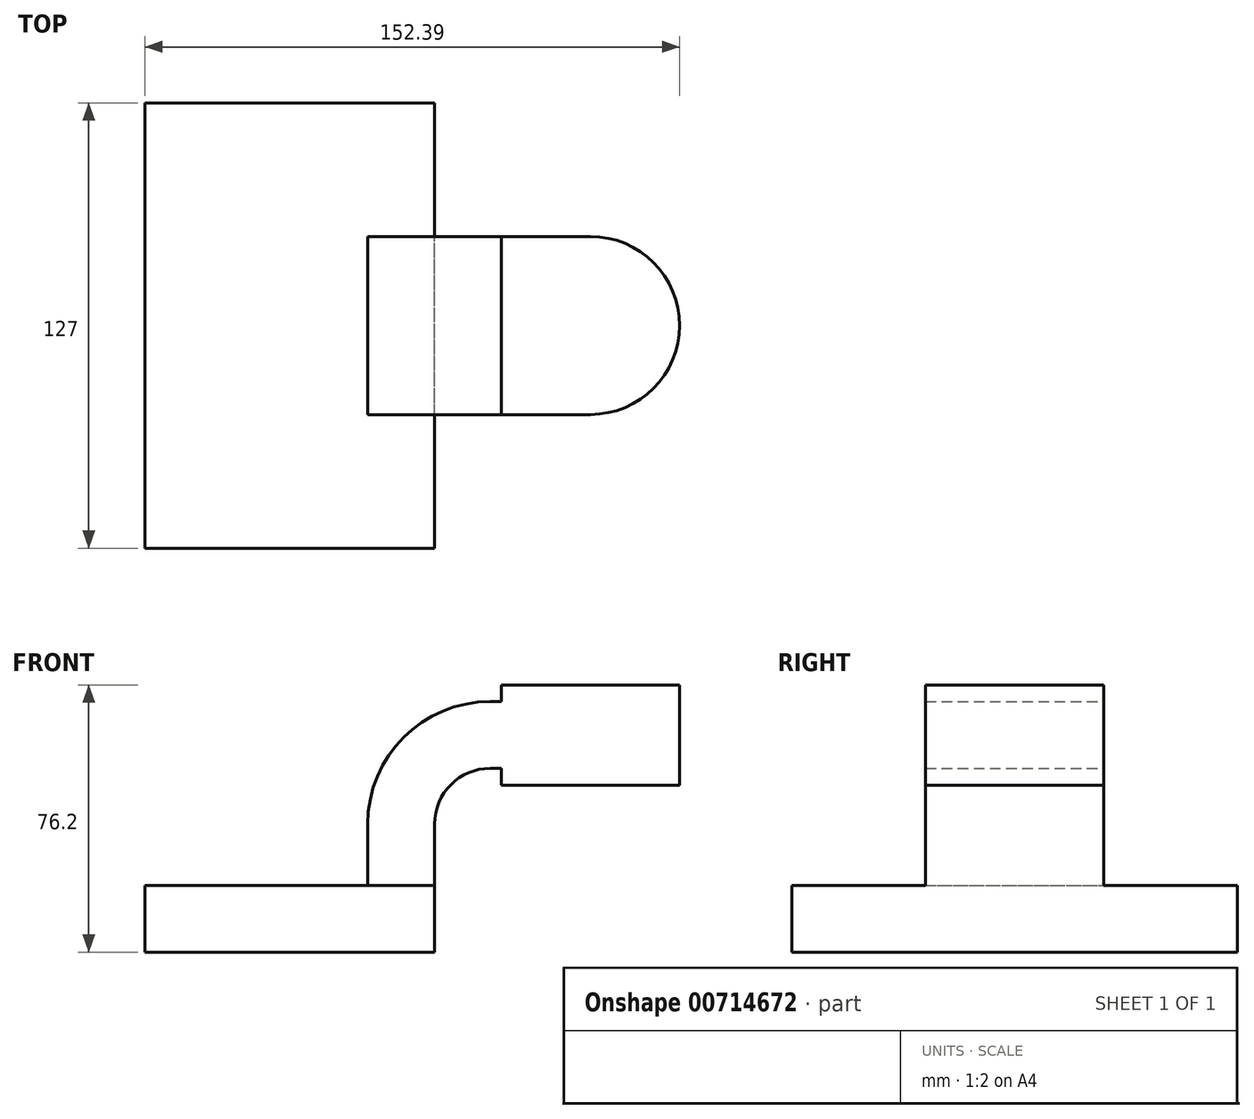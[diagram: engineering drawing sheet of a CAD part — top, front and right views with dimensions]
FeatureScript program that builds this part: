
annotation { "Feature Type Name" : "Feature", "Feature Type Description" : "" }
export const myFeature = defineFeature(function(context is Context, id is Id, definition is map)
    precondition{}
    {
        {
            var Q0;
            Q0=qCreatedBy(makeId("Front.planeOp"),FACE);
            var sketch = newSketch(context, id + "F0", { "sketchPlane" : qUnion([Q0])});
            skLineSegment(sketch, "E0.bottom", {"start": v(-41.28, -9.53) * mm, "end": v(41.28, -9.53) * mm});
            skLineSegment(sketch, "E0.top", {"start": v(-41.28, 9.53) * mm, "end": v(41.28, 9.53) * mm});
            skLineSegment(sketch, "E0.left", {"start": v(-41.28, -9.53) * mm, "end": v(-41.28, 9.53) * mm});
            skLineSegment(sketch, "E0.right", {"start": v(41.28, -9.53) * mm, "end": v(41.28, 9.53) * mm});
            skPoint(sketch, "E0.middle", {"position": v(0, 0) * mm});
            skLineSegment(sketch, "E1.bottom", {"start": v(60.32, 38.1) * mm, "end": v(111.12, 38.1) * mm});
            skLineSegment(sketch, "E1.top", {"start": v(60.32, 66.68) * mm, "end": v(111.12, 66.68) * mm});
            skLineSegment(sketch, "E1.left", {"start": v(60.32, 38.1) * mm, "end": v(60.32, 66.67) * mm});
            skLineSegment(sketch, "E1.right", {"start": v(111.12, 38.1) * mm, "end": v(111.12, 66.67) * mm});
            skPoint(sketch, "E1.middle", {"position": v(85.72, 52.39) * mm});
            skLineSegment(sketch, "E2", {"start": v(41.28, 9.53) * mm, "end": v(41.28, 27) * mm});
            skArc(sketch, "E3", {"start": v(41.27, 27) * mm, "mid": v(45.92, 38.23) * mm, "end": v(57.15, 42.88) * mm});
            skLineSegment(sketch, "E4", {"start": v(57.15, 42.88) * mm, "end": v(85.25, 42.88) * mm});
            skLineSegment(sketch, "E5.0", {"start": v(57.15, 61.93) * mm, "end": v(85.25, 61.93) * mm});
            skArc(sketch, "E5.1", {"start": v(22.22, 27) * mm, "mid": v(32.45, 51.7) * mm, "end": v(57.15, 61.93) * mm});
            skLineSegment(sketch, "E5.2", {"start": v(22.23, 9.53) * mm, "end": v(22.23, 27) * mm});
            skLineSegment(sketch, "E6", {"start": v(85.72, 66.68) * mm, "end": v(85.72, 38.1) * mm});
            skFitSpline(sketch, "E7", {"points": [v(-41.28, 9.53) * mm, v(60.32, 66.67) * mm], "startDerivative": vector(64.63, 87.24) * mm, "endDerivative": vector(129.97, 21.04) * mm});
            skSolve(sketch);
        }
        {
            var Q0;
            Q0=makeQuery(id+"F0.imprint","IMPRINT",FACE,{"disambiguationData":[TD([[makeQuery(id+"F0.imprint","IMPRINT",EDGE,{"derivedFrom":sQuery(id+"F0.wireOp",EDGE,"E0.bottom")}),1.0]])]});
            extrude(context, id + "F1", {"entities" : qUnion([Q0]), "endBound" : BoundingType.SYMMETRIC, "depth" : 127 * mm, "offsetDistance" : 25.4 * mm});
        }
        {
            var Q0;
            {var subQ1=sQuery(id+"F0.wireOp",EDGE,"E2");Q0=makeQuery(id+"F0.imprint","IMPRINT",FACE,{"disambiguationData":[TD([[makeQuery(id+"F0.imprint","IMPRINT",EDGE,{"derivedFrom":subQ1}),1.0]])]});}
            var Q1;
            {var subQ6=sQuery(id+"F0.wireOp",EDGE,"E6");Q1=makeQuery(id+"F0.imprint","IMPRINT",FACE,{"disambiguationData":[TD([[makeQuery(id+"F0.imprint","IMPRINT",EDGE,{"derivedFrom":subQ6}),-1.0]])]});}
            extrude(context, id + "F2", {"entities" : qUnion([Q0, Q1]), "operationType" : NewBodyOperationType.ADD, "endBound" : BoundingType.SYMMETRIC, "depth" : 50.8 * mm, "offsetDistance" : 25.4 * mm});
        }
        {
            var Q0;
            {var subQ0=sQuery(id+"F0.wireOp",EDGE,"E5.1");Q0=makeQuery(id+"F0.imprint","IMPRINT",FACE,{"disambiguationData":[TD([[makeQuery(id+"F0.imprint","IMPRINT",EDGE,{"derivedFrom":subQ0}),1.0]])]});}
            extrude(context, id + "F3", {"entities" : qUnion([Q0]), "operationType" : NewBodyOperationType.ADD, "endBound" : BoundingType.SYMMETRIC, "depth" : 15.88 * mm, "offsetDistance" : 25.4 * mm});
        }
        {
            var Q0;
            {var subQ0=sQuery(id+"F0.wireOp",EDGE,"E1.right");Q0=makeQuery(id+"F0.imprint","IMPRINT",FACE,{"disambiguationData":[TD([[makeQuery(id+"F0.imprint","IMPRINT",EDGE,{"derivedFrom":subQ0}),1.0]])]});}
            var Q1;
            Q1=sQuery(id+"F0.wireOp",EDGE,"E6");
            revolve(context, id + "F4", {"operationType" : NewBodyOperationType.ADD, "surfaceOperationType" : NewSurfaceOperationType.NEW, "entities" : qUnion([Q0]), "axis" : qUnion([Q1]), "revolveType" : RevolveType.FULL});
        }
    });
